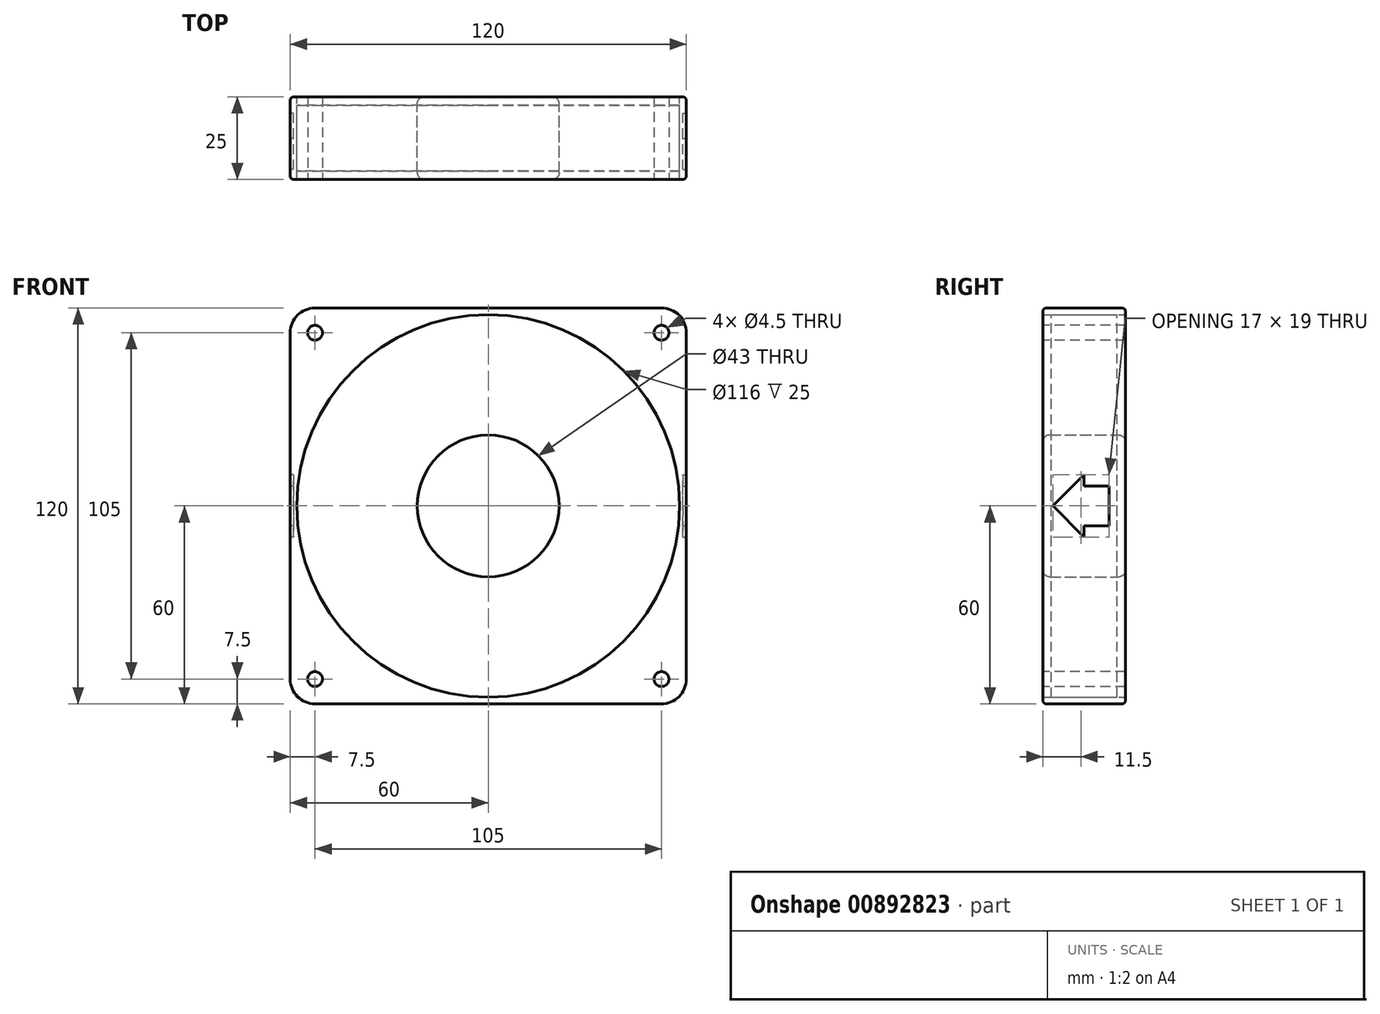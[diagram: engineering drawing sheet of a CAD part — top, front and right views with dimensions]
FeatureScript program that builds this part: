
annotation { "Feature Type Name" : "Feature", "Feature Type Description" : "" }
export const myFeature = defineFeature(function(context is Context, id is Id, definition is map)
    precondition{}
    {
        {
            var Q0;
            Q0=qCreatedBy(makeId("Front.planeOp"),FACE);
            var sketch = newSketch(context, id + "F0", { "sketchPlane" : qUnion([Q0])});
            skLineSegment(sketch, "E0.bottom", {"start": v(-52.5, 60) * mm, "end": v(52.5, 60) * mm});
            skLineSegment(sketch, "E0.top", {"start": v(-52.5, -60) * mm, "end": v(52.5, -60) * mm});
            skLineSegment(sketch, "E0.left", {"start": v(-60, 52.5) * mm, "end": v(-60, -52.5) * mm});
            skLineSegment(sketch, "E0.right", {"start": v(60, 52.5) * mm, "end": v(60, -52.5) * mm});
            skPoint(sketch, "E0.middle", {"position": v(0, 0) * mm});
            skPoint(sketch, "E1.visualSharp", {"position": v(-60, 60) * mm});
            skArc(sketch, "E1.filletArc", {"start": v(-52.5, 60) * mm, "mid": v(-57.8, 57.8) * mm, "end": v(-60, 52.5) * mm});
            skPoint(sketch, "E2.visualSharp", {"position": v(60, 60) * mm});
            skArc(sketch, "E2.filletArc", {"start": v(60, 52.5) * mm, "mid": v(57.8, 57.8) * mm, "end": v(52.5, 60) * mm});
            skPoint(sketch, "E3.visualSharp", {"position": v(60, -60) * mm});
            skArc(sketch, "E3.filletArc", {"start": v(52.5, -60) * mm, "mid": v(57.8, -57.8) * mm, "end": v(60, -52.5) * mm});
            skPoint(sketch, "E4.visualSharp", {"position": v(-60, -60) * mm});
            skArc(sketch, "E4.filletArc", {"start": v(-60, -52.5) * mm, "mid": v(-57.8, -57.8) * mm, "end": v(-52.5, -60) * mm});
            skCircle(sketch, "E5", {"center": v(0, 0) * mm, "radius": 58 * mm});
            skCircle(sketch, "E6", {"center": v(0, 0) * mm, "radius": 21.5 * mm});
            skSolve(sketch);
        }
        {
            var Q0;
            Q0 = qSketchRegion(id + "F0", true);
            var Q1;
            Q1=makeQuery(id+"F0.imprint","IMPRINT",FACE,{"disambiguationData":[TD([[makeQuery(id+"F0.imprint","IMPRINT",EDGE,{"derivedFrom":sQuery(id+"F0.wireOp",EDGE,"E6")}),1.0]])]});
            extrude(context, id + "F1", {"entities" : qUnion([Q0, Q1]), "endBound" : BoundingType.SYMMETRIC, "depth" : 25 * mm, "offsetDistance" : 25 * mm});
        }
        {
            var Q0;
            Q0=makeQuery(id+"F0.imprint","IMPRINT",FACE,{"disambiguationData":[TD([[makeQuery(id+"F0.imprint","IMPRINT",EDGE,{"derivedFrom":sQuery(id+"F0.wireOp",EDGE,"E5")}),1.0]])]});
            extrude(context, id + "F2", {"entities" : qUnion([Q0]), "endBound" : BoundingType.SYMMETRIC, "depth" : 20 * mm, "offsetDistance" : 25 * mm});
        }
        {
            var Q0;
            Q0=makeQuery(id+"F1.opExtrude","CAP_EDGE",EDGE,{"disambiguationData":[OSD([sQuery(id+"F0.wireOp",EDGE,"E6")])],"isStart":false});
            var Q1;
            Q1=makeQuery(id+"F1.opExtrude","CAP_EDGE",EDGE,{"disambiguationData":[OSD([sQuery(id+"F0.wireOp",EDGE,"E6")])],"isStart":true});
            fillet(context, id + "F3", {"entities" : qUnion([Q0, Q1]), "radius" : 2 * mm, "tangentPropagation" : true, "allowEdgeOverflow" : false});
        }
        {
            var Q0;
            Q0=makeQuery(id+"F1.opExtrude","CAP_EDGE",EDGE,{"disambiguationData":[OSD([sQuery(id+"F0.wireOp",EDGE,"E0.left")])],"isStart":false});
            var Q1;
            Q1=makeQuery(id+"F1.opExtrude","CAP_EDGE",EDGE,{"disambiguationData":[OSD([sQuery(id+"F0.wireOp",EDGE,"E4.filletArc")])],"isStart":false});
            var Q2;
            Q2=makeQuery(id+"F1.opExtrude","CAP_EDGE",EDGE,{"disambiguationData":[OSD([sQuery(id+"F0.wireOp",EDGE,"E0.top")])],"isStart":false});
            var Q3;
            Q3=makeQuery(id+"F1.opExtrude","CAP_EDGE",EDGE,{"disambiguationData":[OSD([sQuery(id+"F0.wireOp",EDGE,"E3.filletArc")])],"isStart":false});
            var Q4;
            Q4=makeQuery(id+"F1.opExtrude","CAP_EDGE",EDGE,{"disambiguationData":[OSD([sQuery(id+"F0.wireOp",EDGE,"E0.right")])],"isStart":false});
            var Q5;
            Q5=makeQuery(id+"F1.opExtrude","CAP_EDGE",EDGE,{"disambiguationData":[OSD([sQuery(id+"F0.wireOp",EDGE,"E2.filletArc")])],"isStart":false});
            var Q6;
            Q6=makeQuery(id+"F1.opExtrude","CAP_EDGE",EDGE,{"disambiguationData":[OSD([sQuery(id+"F0.wireOp",EDGE,"E0.bottom")])],"isStart":false});
            var Q7;
            Q7=makeQuery(id+"F1.opExtrude","CAP_EDGE",EDGE,{"disambiguationData":[OSD([sQuery(id+"F0.wireOp",EDGE,"E1.filletArc")])],"isStart":false});
            var Q8;
            Q8=makeQuery(id+"F1.opExtrude","CAP_EDGE",EDGE,{"disambiguationData":[OSD([sQuery(id+"F0.wireOp",EDGE,"E4.filletArc")])],"isStart":true});
            var Q9;
            Q9=makeQuery(id+"F1.opExtrude","CAP_EDGE",EDGE,{"disambiguationData":[OSD([sQuery(id+"F0.wireOp",EDGE,"E0.top")])],"isStart":true});
            var Q10;
            Q10=makeQuery(id+"F1.opExtrude","CAP_EDGE",EDGE,{"disambiguationData":[OSD([sQuery(id+"F0.wireOp",EDGE,"E3.filletArc")])],"isStart":true});
            var Q11;
            Q11=makeQuery(id+"F1.opExtrude","CAP_EDGE",EDGE,{"disambiguationData":[OSD([sQuery(id+"F0.wireOp",EDGE,"E0.left")])],"isStart":true});
            var Q12;
            Q12=makeQuery(id+"F1.opExtrude","CAP_EDGE",EDGE,{"disambiguationData":[OSD([sQuery(id+"F0.wireOp",EDGE,"E0.right")])],"isStart":true});
            var Q13;
            Q13=makeQuery(id+"F1.opExtrude","CAP_EDGE",EDGE,{"disambiguationData":[OSD([sQuery(id+"F0.wireOp",EDGE,"E2.filletArc")])],"isStart":true});
            var Q14;
            Q14=makeQuery(id+"F1.opExtrude","CAP_EDGE",EDGE,{"disambiguationData":[OSD([sQuery(id+"F0.wireOp",EDGE,"E0.bottom")])],"isStart":true});
            var Q15;
            Q15=makeQuery(id+"F1.opExtrude","CAP_EDGE",EDGE,{"disambiguationData":[OSD([sQuery(id+"F0.wireOp",EDGE,"E1.filletArc")])],"isStart":true});
            fillet(context, id + "F4", {"entities" : qUnion([Q0, Q1, Q2, Q3, Q4, Q5, Q6, Q7, Q8, Q9, Q10, Q11, Q12, Q13, Q14, Q15]), "radius" : 1 * mm, "tangentPropagation" : true, "allowEdgeOverflow" : false});
        }
        {
            var Q0;
            Q0=makeQuery(id+"F1.opExtrude","CAP_FACE",FACE,{"disambiguationData":[OSD([sQuery(id+"F0.wireOp",EDGE,"E0.bottom"),sQuery(id+"F0.wireOp",EDGE,"E0.top"),sQuery(id+"F0.wireOp",EDGE,"E0.left"),sQuery(id+"F0.wireOp",EDGE,"E0.right"),sQuery(id+"F0.wireOp",EDGE,"E1.filletArc"),sQuery(id+"F0.wireOp",EDGE,"E2.filletArc"),sQuery(id+"F0.wireOp",EDGE,"E3.filletArc"),sQuery(id+"F0.wireOp",EDGE,"E4.filletArc"),sQuery(id+"F0.wireOp",EDGE,"E5")])],"isStart":false});
            var sketch = newSketch(context, id + "F5", { "sketchPlane" : qUnion([Q0])});
            skPoint(sketch, "E7", {"position": v(-52.5, 52.5) * mm});
            skPoint(sketch, "E8", {"position": v(52.5, 52.5) * mm});
            skPoint(sketch, "E9", {"position": v(52.5, -52.5) * mm});
            skPoint(sketch, "E10", {"position": v(-52.5, -52.5) * mm});
            skSolve(sketch);
        }
        {
            var Q0;
            Q0=sQuery(id+"F5.wireOp",VERTEX,"E7");
            var Q1;
            Q1=sQuery(id+"F5.wireOp",VERTEX,"E8");
            var Q2;
            Q2=sQuery(id+"F5.wireOp",VERTEX,"E9");
            var Q3;
            Q3=sQuery(id+"F5.wireOp",VERTEX,"E10");
            var Q4;
            Q4=makeQuery(id+"F1.opExtrude","SWEPT_BODY",BODY,{"disambiguationData":[OSD([sQuery(id+"F0.wireOp",EDGE,"E0.bottom"),sQuery(id+"F0.wireOp",EDGE,"E0.top"),sQuery(id+"F0.wireOp",EDGE,"E0.left"),sQuery(id+"F0.wireOp",EDGE,"E0.right"),sQuery(id+"F0.wireOp",EDGE,"E1.filletArc"),sQuery(id+"F0.wireOp",EDGE,"E2.filletArc"),sQuery(id+"F0.wireOp",EDGE,"E3.filletArc"),sQuery(id+"F0.wireOp",EDGE,"E4.filletArc"),sQuery(id+"F0.wireOp",EDGE,"E5")])]});
            hole(context, id + "F6", {"style" : HoleStyle.SIMPLE, "endStyle" : HoleEndStyle.THROUGH, "holeDiameter" : 4.5 * mm, "majorDiameter" : 5 * mm, "isTappedThrough" : true, "tappedDepth" : 12 * mm, "tapClearance" : 3, "locations" : qUnion([Q0, Q1, Q2, Q3]), "scope" : qUnion([Q4])});
        }
        {
            var Q0;
            Q0=makeQuery(id+"F1.opExtrude","SWEPT_FACE",FACE,{"disambiguationData":[OSD([sQuery(id+"F0.wireOp",EDGE,"E0.left")])]});
            var sketch = newSketch(context, id + "F7", { "sketchPlane" : qUnion([Q0])});
            skLineSegment(sketch, "E11", {"start": v(9.5, 0) * mm, "end": v(0, 9.5) * mm});
            skLineSegment(sketch, "E12", {"start": v(0, 9.5) * mm, "end": v(0, 6) * mm});
            skLineSegment(sketch, "E13", {"start": v(0, 6) * mm, "end": v(-7.5, 6) * mm});
            skLineSegment(sketch, "E14", {"start": v(-7.5, 6) * mm, "end": v(-7.5, 0) * mm});
            skLineSegment(sketch, "E15.MirrorCS", {"start": v(-7.5, -6) * mm, "end": v(-7.5, 0) * mm});
            skLineSegment(sketch, "E16.MirrorCS", {"start": v(0, -6) * mm, "end": v(-7.5, -6) * mm});
            skLineSegment(sketch, "E17.MirrorCS", {"start": v(0, -9.5) * mm, "end": v(0, -6) * mm});
            skLineSegment(sketch, "E18.MirrorCS", {"start": v(9.5, 0) * mm, "end": v(0, -9.5) * mm});
            skSolve(sketch);
        }
        {
            var Q0;
            Q0=makeQuery(id+"F7.imprint","IMPRINT",FACE,{"disambiguationData":[TD([[makeQuery(id+"F7.imprint","IMPRINT",EDGE,{"derivedFrom":sQuery(id+"F7.wireOp",EDGE,"E11")}),1.0]])]});
            extrude(context, id + "F8", {"entities" : qUnion([Q0]), "operationType" : NewBodyOperationType.REMOVE, "oppositeDirection" : true, "depth" : 1 * mm, "offsetDistance" : 25 * mm});
        }
        {
            var Q0;
            Q0=makeQuery(id+"F1.opExtrude","SWEPT_FACE",FACE,{"disambiguationData":[OSD([sQuery(id+"F0.wireOp",EDGE,"E0.right")])]});
            var sketch = newSketch(context, id + "F9", { "sketchPlane" : qUnion([Q0])});
            skLineSegment(sketch, "E19", {"start": v(-9.5, 0) * mm, "end": v(0, 9.5) * mm});
            skLineSegment(sketch, "E20", {"start": v(0, 9.5) * mm, "end": v(0, 6) * mm});
            skLineSegment(sketch, "E21", {"start": v(0, 6) * mm, "end": v(7.5, 6) * mm});
            skLineSegment(sketch, "E22", {"start": v(7.5, 6) * mm, "end": v(7.5, 0) * mm});
            skLineSegment(sketch, "E23.MirrorCS", {"start": v(-9.5, 0) * mm, "end": v(0, -9.5) * mm});
            skLineSegment(sketch, "E24.MirrorCS", {"start": v(0, -9.5) * mm, "end": v(0, -6) * mm});
            skLineSegment(sketch, "E25.MirrorCS", {"start": v(0, -6) * mm, "end": v(7.5, -6) * mm});
            skLineSegment(sketch, "E26.MirrorCS", {"start": v(7.5, -6) * mm, "end": v(7.5, 0) * mm});
            skSolve(sketch);
        }
        {
            var Q0;
            Q0=makeQuery(id+"F9.imprint","IMPRINT",FACE,{"disambiguationData":[TD([[makeQuery(id+"F9.imprint","IMPRINT",EDGE,{"derivedFrom":sQuery(id+"F9.wireOp",EDGE,"E19")}),-1.0]])]});
            extrude(context, id + "F10", {"entities" : qUnion([Q0]), "operationType" : NewBodyOperationType.REMOVE, "oppositeDirection" : true, "depth" : 1 * mm, "offsetDistance" : 25 * mm});
        }
    });
